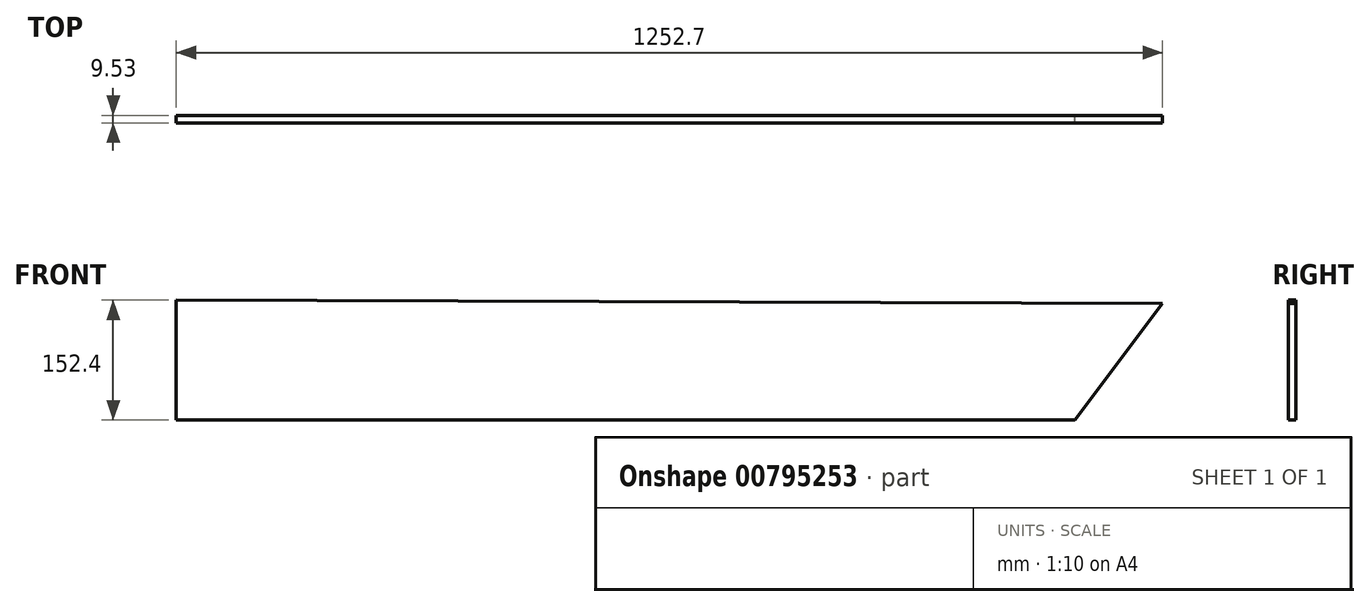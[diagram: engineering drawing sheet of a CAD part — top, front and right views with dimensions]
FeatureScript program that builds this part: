
annotation { "Feature Type Name" : "Feature", "Feature Type Description" : "" }
export const myFeature = defineFeature(function(context is Context, id is Id, definition is map)
    precondition{}
    {
        {
            var Q0;
            Q0=qCreatedBy(makeId("Front.planeOp"),FACE);
            var sketch = newSketch(context, id + "F0", { "sketchPlane" : qUnion([Q0])});
            skLineSegment(sketch, "E0", {"start": v(603.73, 97.4) * mm, "end": v(492.29, -50.52) * mm});
            skLineSegment(sketch, "E1", {"start": v(492.29, -50.52) * mm, "end": v(-648.97, -50.52) * mm});
            skLineSegment(sketch, "E2", {"start": v(-648.97, -50.52) * mm, "end": v(-648.97, 101.88) * mm});
            skLineSegment(sketch, "E3", {"start": v(-648.97, 101.88) * mm, "end": v(603.73, 97.4) * mm});
            skSolve(sketch);
        }
        {
            var Q0;
            Q0 = qSketchRegion(id + "F0", true);
            extrude(context, id + "F1", {"entities" : qUnion([Q0]), "depth" : 9.52 * mm, "offsetDistance" : 25.4 * mm});
        }
    });
